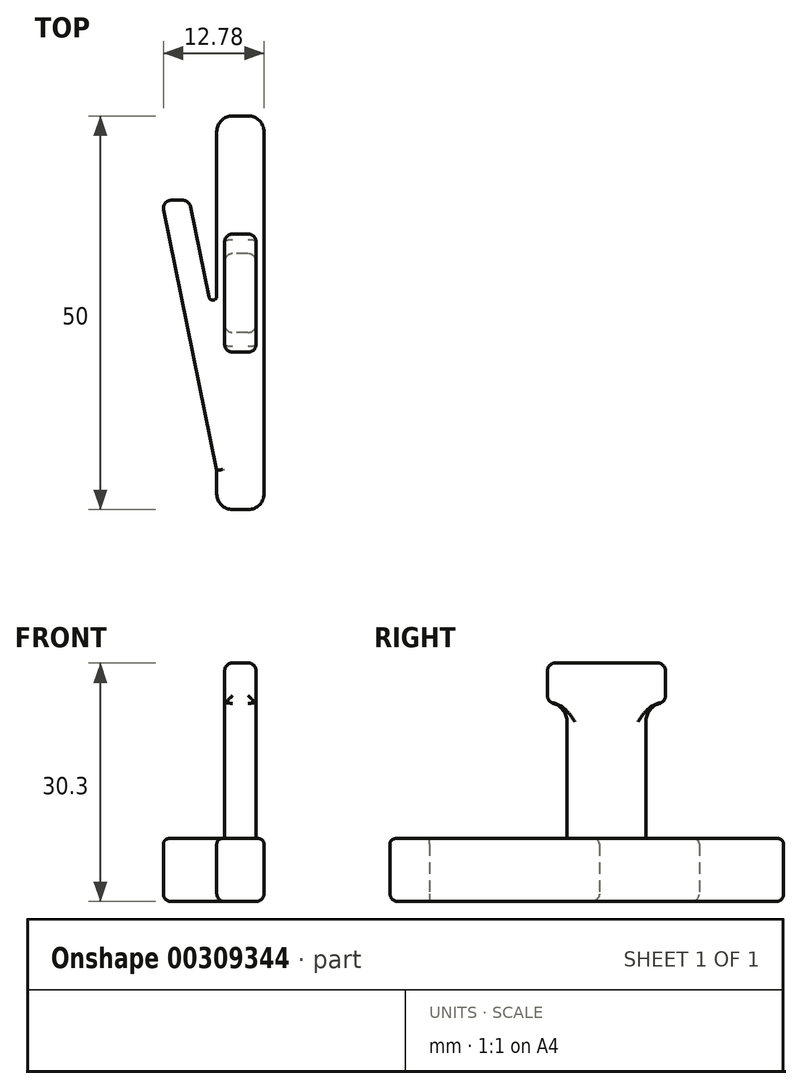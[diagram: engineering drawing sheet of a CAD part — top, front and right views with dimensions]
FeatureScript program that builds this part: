
annotation { "Feature Type Name" : "Feature", "Feature Type Description" : "" }
export const myFeature = defineFeature(function(context is Context, id is Id, definition is map)
    precondition{}
    {
        {
            var Q0;
            Q0=qCreatedBy(makeId("Top.planeOp"),FACE);
            var sketch = newSketch(context, id + "F0", { "sketchPlane" : qUnion([Q0])});
            skLineSegment(sketch, "E0.bottom", {"start": v(0, 0) * mm, "end": v(6, 0) * mm});
            skLineSegment(sketch, "E0.top", {"start": v(0, -50) * mm, "end": v(6, -50) * mm});
            skLineSegment(sketch, "E0.left", {"start": v(0, 0) * mm, "end": v(0, -50) * mm});
            skLineSegment(sketch, "E0.right", {"start": v(6, 0) * mm, "end": v(6, -50) * mm});
            skLineSegment(sketch, "E1", {"start": v(0, -50) * mm, "end": v(0, -45) * mm});
            skLineSegment(sketch, "E2", {"start": v(0, -45) * mm, "end": v(-7, -45) * mm});
            skLineSegment(sketch, "E3", {"start": v(0, -45) * mm, "end": v(-7, -10.7) * mm});
            skLineSegment(sketch, "E4", {"start": v(-7, -10.7) * mm, "end": v(-3.5, -10.7) * mm});
            skLineSegment(sketch, "E5", {"start": v(-3.5, -10.7) * mm, "end": v(0, -27.85) * mm});
            skSolve(sketch);
        }
        {
            var Q0;
            Q0=qSketchRegion(id+"F0",true);
            extrude(context, id + "F1", {"entities" : qUnion([Q0]), "depth" : 8 * mm});
        }
        {
            var Q0;
            Q0=makeQuery(id+"F1.opExtrude","SWEPT_EDGE",EDGE,{"disambiguationData":[OSD([sQuery(id+"F0.wireOp",EDGE,"E3"),sQuery(id+"F0.wireOp",EDGE,"E4")])]});
            var Q1;
            Q1=makeQuery(id+"F1.opExtrude","SWEPT_EDGE",EDGE,{"disambiguationData":[OSD([sQuery(id+"F0.wireOp",EDGE,"E4"),sQuery(id+"F0.wireOp",EDGE,"E5")])]});
            fillet(context, id + "F2", {"entities" : qUnion([Q0, Q1]), "radius" : 1 * mm, "tangentPropagation" : true, "allowEdgeOverflow" : false});
        }
        {
            var Q0;
            Q0=makeQuery(id+"F1.opExtrude","SWEPT_EDGE",EDGE,{"disambiguationData":[OSD([sQuery(id+"F0.wireOp",EDGE,"E0.left"),sQuery(id+"F0.wireOp",EDGE,"E5")])]});
            fillet(context, id + "F3", {"entities" : qUnion([Q0]), "radius" : .5 * mm, "tangentPropagation" : true, "allowEdgeOverflow" : false});
        }
        {
            var Q0;
            Q0=makeQuery(id+"F1.opExtrude","SWEPT_EDGE",EDGE,{"disambiguationData":[OSD([sQuery(id+"F0.wireOp",EDGE,"E0.bottom"),sQuery(id+"F0.wireOp",EDGE,"E0.left")])]});
            var Q1;
            Q1=makeQuery(id+"F1.opExtrude","SWEPT_EDGE",EDGE,{"disambiguationData":[OSD([sQuery(id+"F0.wireOp",EDGE,"E0.bottom"),sQuery(id+"F0.wireOp",EDGE,"E0.right")])]});
            var Q2;
            Q2=makeQuery(id+"F1.opExtrude","SWEPT_EDGE",EDGE,{"disambiguationData":[OSD([sQuery(id+"F0.wireOp",EDGE,"E0.top"),sQuery(id+"F0.wireOp",EDGE,"E0.right")])]});
            var Q3;
            Q3=makeQuery(id+"F1.opExtrude","SWEPT_EDGE",EDGE,{"disambiguationData":[OSD([sQuery(id+"F0.wireOp",EDGE,"E0.top"),sQuery(id+"F0.wireOp",EDGE,"E1")])]});
            fillet(context, id + "F4", {"entities" : qUnion([Q0, Q1, Q2, Q3]), "radius" : 2 * mm, "tangentPropagation" : true, "allowEdgeOverflow" : false});
        }
        {
            var Q0;
            Q0=makeQuery(id+"F1.opExtrude","CAP_FACE",FACE,{"disambiguationData":[OSD([sQuery(id+"F0.wireOp",EDGE,"E0.bottom"),sQuery(id+"F0.wireOp",EDGE,"E0.top"),sQuery(id+"F0.wireOp",EDGE,"E0.left"),sQuery(id+"F0.wireOp",EDGE,"E0.right"),sQuery(id+"F0.wireOp",EDGE,"E1"),sQuery(id+"F0.wireOp",EDGE,"E3"),sQuery(id+"F0.wireOp",EDGE,"E4"),sQuery(id+"F0.wireOp",EDGE,"E5")])],"isStart":false});
            fillet(context, id + "F5", {"entities" : qUnion([Q0]), "radius" : .7 * mm, "allowEdgeOverflow" : false});
        }
        {
            var Q0;
            Q0=makeQuery(id+"F1.opExtrude","SWEPT_FACE",FACE,{"disambiguationData":[OSD([sQuery(id+"F0.wireOp",EDGE,"E0.right")])]});
            var sketch = newSketch(context, id + "F6", { "sketchPlane" : qUnion([Q0])});
            skLineSegment(sketch, "E6.bottom", {"start": v(-27.5, 5.76) * mm, "end": v(-17.5, 5.76) * mm});
            skLineSegment(sketch, "E6.top", {"start": v(-27.5, 25.76) * mm, "end": v(-17.5, 25.76) * mm});
            skLineSegment(sketch, "E6.left", {"start": v(-27.5, 5.76) * mm, "end": v(-27.5, 25.76) * mm});
            skLineSegment(sketch, "E6.right", {"start": v(-17.5, 5.76) * mm, "end": v(-17.5, 25.76) * mm});
            skLineSegment(sketch, "E7.bottom", {"start": v(-30, 25.3) * mm, "end": v(-15, 25.3) * mm});
            skLineSegment(sketch, "E7.top", {"start": v(-30, 30.3) * mm, "end": v(-15, 30.3) * mm});
            skLineSegment(sketch, "E7.left", {"start": v(-30, 25.3) * mm, "end": v(-30, 30.3) * mm});
            skLineSegment(sketch, "E7.right", {"start": v(-15, 25.3) * mm, "end": v(-15, 30.3) * mm});
            skLineSegment(sketch, "E8", {"start": v(-27.5, 5.76) * mm, "end": v(-27.5, 4.76) * mm});
            skLineSegment(sketch, "E9", {"start": v(-27.5, 4.76) * mm, "end": v(-17.5, 4.76) * mm});
            skLineSegment(sketch, "E10", {"start": v(-17.5, 4.76) * mm, "end": v(-17.5, 5.76) * mm});
            skSolve(sketch);
        }
        {
            var Q0;
            {var subQ1=sQuery(id+"F6.wireOp",EDGE,"E6.top");Q0=makeQuery(id+"F6.imprint","IMPRINT",FACE,{"disambiguationData":[TD([[makeQuery(id+"F6.imprint","IMPRINT",EDGE,{"derivedFrom":subQ1}),1.0]])]});}
            var Q1;
            {var subQ0=sQuery(id+"F6.wireOp",EDGE,"E6.bottom");Q1=makeQuery(id+"F6.imprint","IMPRINT",FACE,{"disambiguationData":[TD([[makeQuery(id+"F6.imprint","IMPRINT",EDGE,{"derivedFrom":subQ0}),1.0]])]});}
            var Q2;
            {var subQ0=sQuery(id+"F6.wireOp",EDGE,"E6.top");Q2=makeQuery(id+"F6.imprint","IMPRINT",FACE,{"disambiguationData":[TD([[makeQuery(id+"F6.imprint","IMPRINT",EDGE,{"derivedFrom":subQ0}),-1.0]])]});}
            var Q3;
            {var subQ0=sQuery(id+"F6.wireOp",EDGE,"E7.bottom");var subQ1=sQuery(id+"F6.wireOp",EDGE,"E6.left");var subQ2=makeQuery(id+"F6.imprint","INTERSECT",VERTEX,{"derivedFrom":[subQ1,subQ0]});Q3=makeQuery(id+"F6.imprint","IMPRINT",FACE,{"disambiguationData":[TD([[makeQuery(id+"F6.imprint","IMPRINT",EDGE,{"disambiguationData":[TD([[subQ2,-1.0]])],"derivedFrom":subQ0}),-1.0]])]});}
            extrude(context, id + "F7", {"entities" : qUnion([Q0, Q1, Q2, Q3]), "operationType" : NewBodyOperationType.ADD, "oppositeDirection" : true, "depth" : 5 * mm, "hasSecondDirection" : true, "secondDirectionOppositeDirection" : true, "secondDirectionDepth" : 1 * mm});
        }
        {
            var Q0;
            Q0=makeQuery(id+"F7.opExtrude","CAP_EDGE",EDGE,{"disambiguationData":[OSD([sQuery(id+"F6.wireOp",EDGE,"E6.right")])],"isStart":false});
            var Q1;
            Q1=makeQuery(id+"F7.opExtrude","CAP_EDGE",EDGE,{"disambiguationData":[OSD([sQuery(id+"F6.wireOp",EDGE,"E6.right")])],"isStart":true});
            var Q2;
            Q2=makeQuery(id+"F7.opExtrude","CAP_EDGE",EDGE,{"disambiguationData":[OSD([sQuery(id+"F6.wireOp",EDGE,"E6.left")])],"isStart":true});
            var Q3;
            Q3=makeQuery(id+"F7.opExtrude","CAP_EDGE",EDGE,{"disambiguationData":[OSD([sQuery(id+"F6.wireOp",EDGE,"E6.left")])],"isStart":false});
            var Q4;
            Q4=makeQuery(id+"F7.opExtrude","SWEPT_EDGE",EDGE,{"disambiguationData":[OSD([sQuery(id+"F6.wireOp",EDGE,"E7.top"),sQuery(id+"F6.wireOp",EDGE,"E7.right")])]});
            var Q5;
            Q5=makeQuery(id+"F7.opExtrude","SWEPT_EDGE",EDGE,{"disambiguationData":[OSD([sQuery(id+"F6.wireOp",EDGE,"E7.top"),sQuery(id+"F6.wireOp",EDGE,"E7.left")])]});
            fillet(context, id + "F8", {"entities" : qUnion([Q0, Q1, Q2, Q3, Q4, Q5]), "radius" : 1 * mm, "allowEdgeOverflow" : false});
        }
        {
            var Q0;
            Q0=makeQuery(id+"F7.opExtrude","SWEPT_EDGE",EDGE,{"disambiguationData":[OSD([sQuery(id+"F6.wireOp",EDGE,"E6.right"),sQuery(id+"F6.wireOp",EDGE,"E7.bottom")])]});
            var Q1;
            Q1=makeQuery(id+"F7.opExtrude","SWEPT_EDGE",EDGE,{"disambiguationData":[OSD([sQuery(id+"F6.wireOp",EDGE,"E6.left"),sQuery(id+"F6.wireOp",EDGE,"E7.bottom")])]});
            fillet(context, id + "F9", {"entities" : qUnion([Q0, Q1]), "radius" : 2.5 * mm, "tangentPropagation" : true, "allowEdgeOverflow" : false});
        }
        {
            var Q0;
            Q0=makeQuery(id+"F7.opExtrude","CAP_EDGE",EDGE,{"disambiguationData":[OSD([sQuery(id+"F6.wireOp",EDGE,"E7.top")])],"isStart":false});
            var Q1;
            Q1=makeQuery(id+"F7.opExtrude","CAP_EDGE",EDGE,{"disambiguationData":[OSD([sQuery(id+"F6.wireOp",EDGE,"E7.top")])],"isStart":true});
            var Q2;
            Q2=makeQuery(id+"F7.opExtrude","CAP_EDGE",EDGE,{"disambiguationData":[OSD([sQuery(id+"F6.wireOp",EDGE,"E7.right")])],"isStart":false});
            var Q3;
            Q3=makeQuery(id+"F7.opExtrude","CAP_EDGE",EDGE,{"disambiguationData":[OSD([sQuery(id+"F6.wireOp",EDGE,"E7.right")])],"isStart":true});
            var Q4;
            Q4=makeQuery(id+"F9.opFillet","BLEND_EDGE",EDGE,{"blendedFrom":[makeQuery(id+"F7.opExtrude","SWEPT_EDGE",EDGE,{"disambiguationData":[OSD([sQuery(id+"F6.wireOp",EDGE,"E6.right"),sQuery(id+"F6.wireOp",EDGE,"E7.bottom")])]}),makeQuery(id+"F7.opExtrude","SWEPT_FACE",FACE,{"disambiguationData":[OSD([sQuery(id+"F6.wireOp",EDGE,"E7.right")])]})],"blendedInto":[makeQuery(id+"F7.opExtrude","SWEPT_FACE",FACE,{"disambiguationData":[OSD([sQuery(id+"F6.wireOp",EDGE,"E7.right")])]})]});
            var Q5;
            Q5=makeQuery(id+"F7.opExtrude","CAP_EDGE",EDGE,{"disambiguationData":[OSD([sQuery(id+"F6.wireOp",EDGE,"E7.left")])],"isStart":false});
            var Q6;
            Q6=makeQuery(id+"F7.opExtrude","CAP_EDGE",EDGE,{"disambiguationData":[OSD([sQuery(id+"F6.wireOp",EDGE,"E7.left")])],"isStart":true});
            var Q7;
            Q7=makeQuery(id+"F9.opFillet","BLEND_EDGE",EDGE,{"blendedFrom":[makeQuery(id+"F7.opExtrude","SWEPT_EDGE",EDGE,{"disambiguationData":[OSD([sQuery(id+"F6.wireOp",EDGE,"E6.left"),sQuery(id+"F6.wireOp",EDGE,"E7.bottom")])]}),makeQuery(id+"F7.opExtrude","SWEPT_FACE",FACE,{"disambiguationData":[OSD([sQuery(id+"F6.wireOp",EDGE,"E7.left")])]})],"blendedInto":[makeQuery(id+"F7.opExtrude","SWEPT_FACE",FACE,{"disambiguationData":[OSD([sQuery(id+"F6.wireOp",EDGE,"E7.left")])]})]});
            fillet(context, id + "F10", {"entities" : qUnion([Q0, Q1, Q2, Q3, Q4, Q5, Q6, Q7]), "radius" : 1 * mm, "allowEdgeOverflow" : false});
        }
        {
            var Q0;
            Q0=makeQuery(id+"F1.opExtrude","CAP_FACE",FACE,{"disambiguationData":[OSD([sQuery(id+"F0.wireOp",EDGE,"E0.bottom"),sQuery(id+"F0.wireOp",EDGE,"E0.top"),sQuery(id+"F0.wireOp",EDGE,"E0.left"),sQuery(id+"F0.wireOp",EDGE,"E0.right"),sQuery(id+"F0.wireOp",EDGE,"E1"),sQuery(id+"F0.wireOp",EDGE,"E3"),sQuery(id+"F0.wireOp",EDGE,"E4"),sQuery(id+"F0.wireOp",EDGE,"E5")])],"isStart":true});
            fillet(context, id + "F11", {"entities" : qUnion([Q0]), "radius" : 1 * mm, "tangentPropagation" : true, "allowEdgeOverflow" : false});
        }
    });
